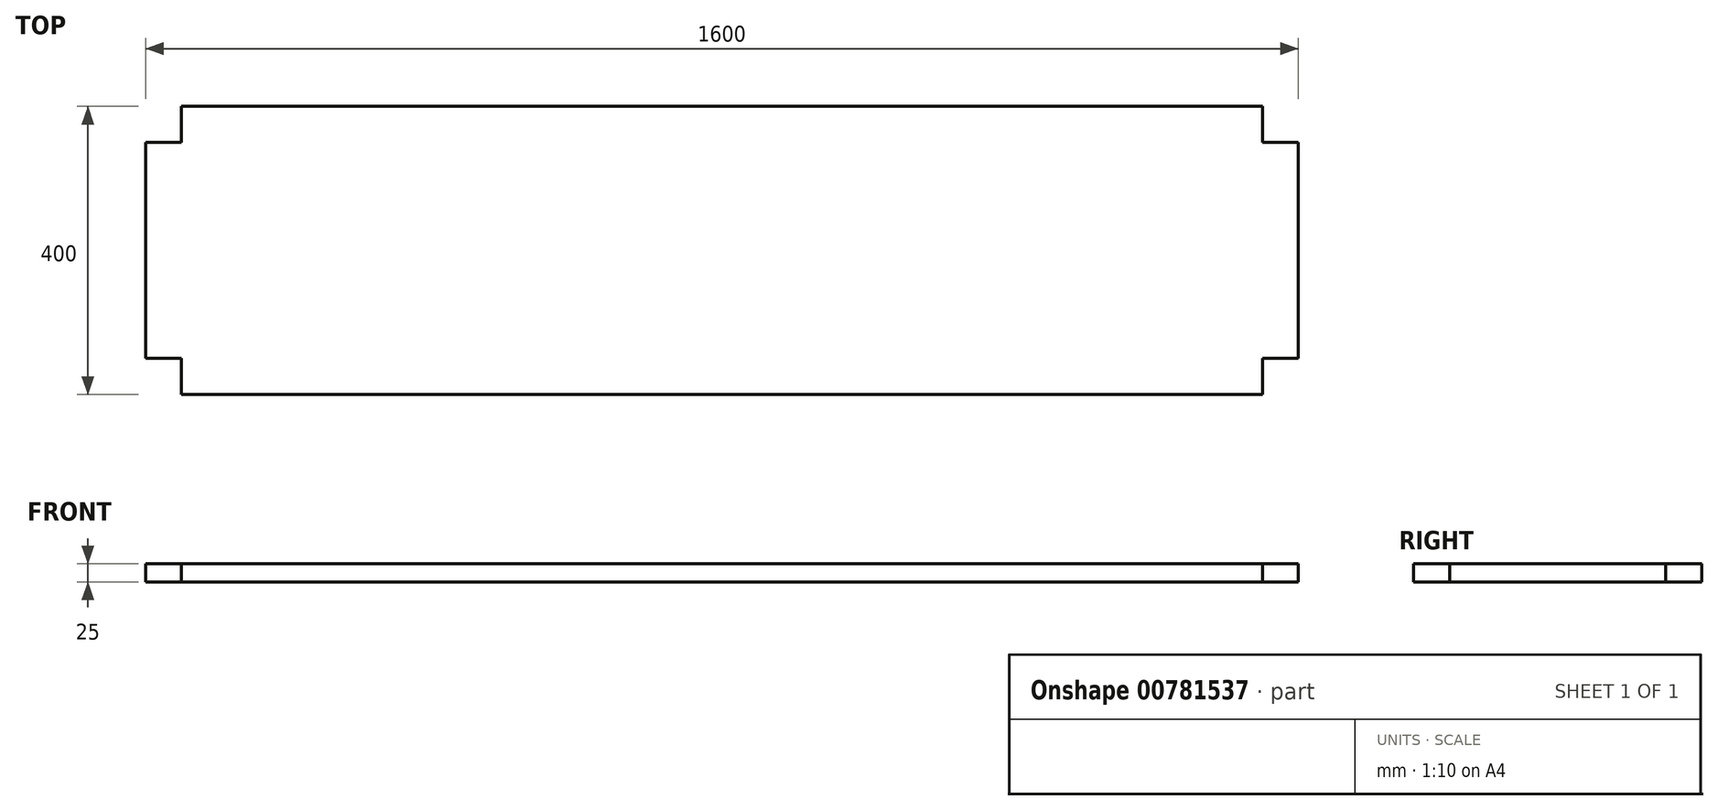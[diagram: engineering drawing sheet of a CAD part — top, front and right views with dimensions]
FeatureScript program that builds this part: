
annotation { "Feature Type Name" : "Feature", "Feature Type Description" : "" }
export const myFeature = defineFeature(function(context is Context, id is Id, definition is map)
    precondition{}
    {
        {
            var Q0;
            Q0=qCreatedBy(makeId("Top.planeOp"),FACE);
            var sketch = newSketch(context, id + "F0", { "sketchPlane" : qUnion([Q0])});
            skLineSegment(sketch, "E0", {"start": v(-800, 0) * mm, "end": v(-800, 150) * mm});
            skLineSegment(sketch, "E1", {"start": v(-800, 150) * mm, "end": v(-750, 150) * mm});
            skLineSegment(sketch, "E2", {"start": v(-750, 150) * mm, "end": v(-750, 200) * mm});
            skLineSegment(sketch, "E3", {"start": v(-750, 200) * mm, "end": v(0, 200) * mm});
            skLineSegment(sketch, "E4", {"start": v(-800, 0) * mm, "end": v(0, 0) * mm, "construction": true});
            skLineSegment(sketch, "E5", {"start": v(0, 0) * mm, "end": v(0, 200) * mm, "construction": true});
            skLineSegment(sketch, "E6.MirrorCS", {"start": v(800, 0) * mm, "end": v(800, 150) * mm});
            skLineSegment(sketch, "E7.MirrorCS", {"start": v(800, 150) * mm, "end": v(750, 150) * mm});
            skLineSegment(sketch, "E8.MirrorCS", {"start": v(750, 200) * mm, "end": v(0, 200) * mm});
            skLineSegment(sketch, "E9.MirrorCS", {"start": v(750, 150) * mm, "end": v(750, 200) * mm});
            skLineSegment(sketch, "E10.MirrorCS", {"start": v(-750, -200) * mm, "end": v(0, -200) * mm});
            skLineSegment(sketch, "E11.MirrorCS", {"start": v(-800, 0) * mm, "end": v(-800, -150) * mm});
            skLineSegment(sketch, "E12.MirrorCS", {"start": v(-800, -150) * mm, "end": v(-750, -150) * mm});
            skLineSegment(sketch, "E13.MirrorCS", {"start": v(-750, -150) * mm, "end": v(-750, -200) * mm});
            skLineSegment(sketch, "E14.MirrorCS", {"start": v(750, -200) * mm, "end": v(0, -200) * mm});
            skLineSegment(sketch, "E15.MirrorCS", {"start": v(750, -150) * mm, "end": v(750, -200) * mm});
            skLineSegment(sketch, "E16.MirrorCS", {"start": v(800, 0) * mm, "end": v(800, -150) * mm});
            skLineSegment(sketch, "E17.MirrorCS", {"start": v(800, -150) * mm, "end": v(750, -150) * mm});
            skSolve(sketch);
        }
        {
            var Q0;
            Q0=makeQuery(id+"F0.imprint","IMPRINT",FACE,{"disambiguationData":[TD([[makeQuery(id+"F0.imprint","IMPRINT",EDGE,{"derivedFrom":sQuery(id+"F0.wireOp",EDGE,"E0")}),-1.0]])]});
            extrude(context, id + "F1", {"entities" : qUnion([Q0]), "depth" : 25 * mm, "offsetDistance" : 25 * mm});
        }
    });
